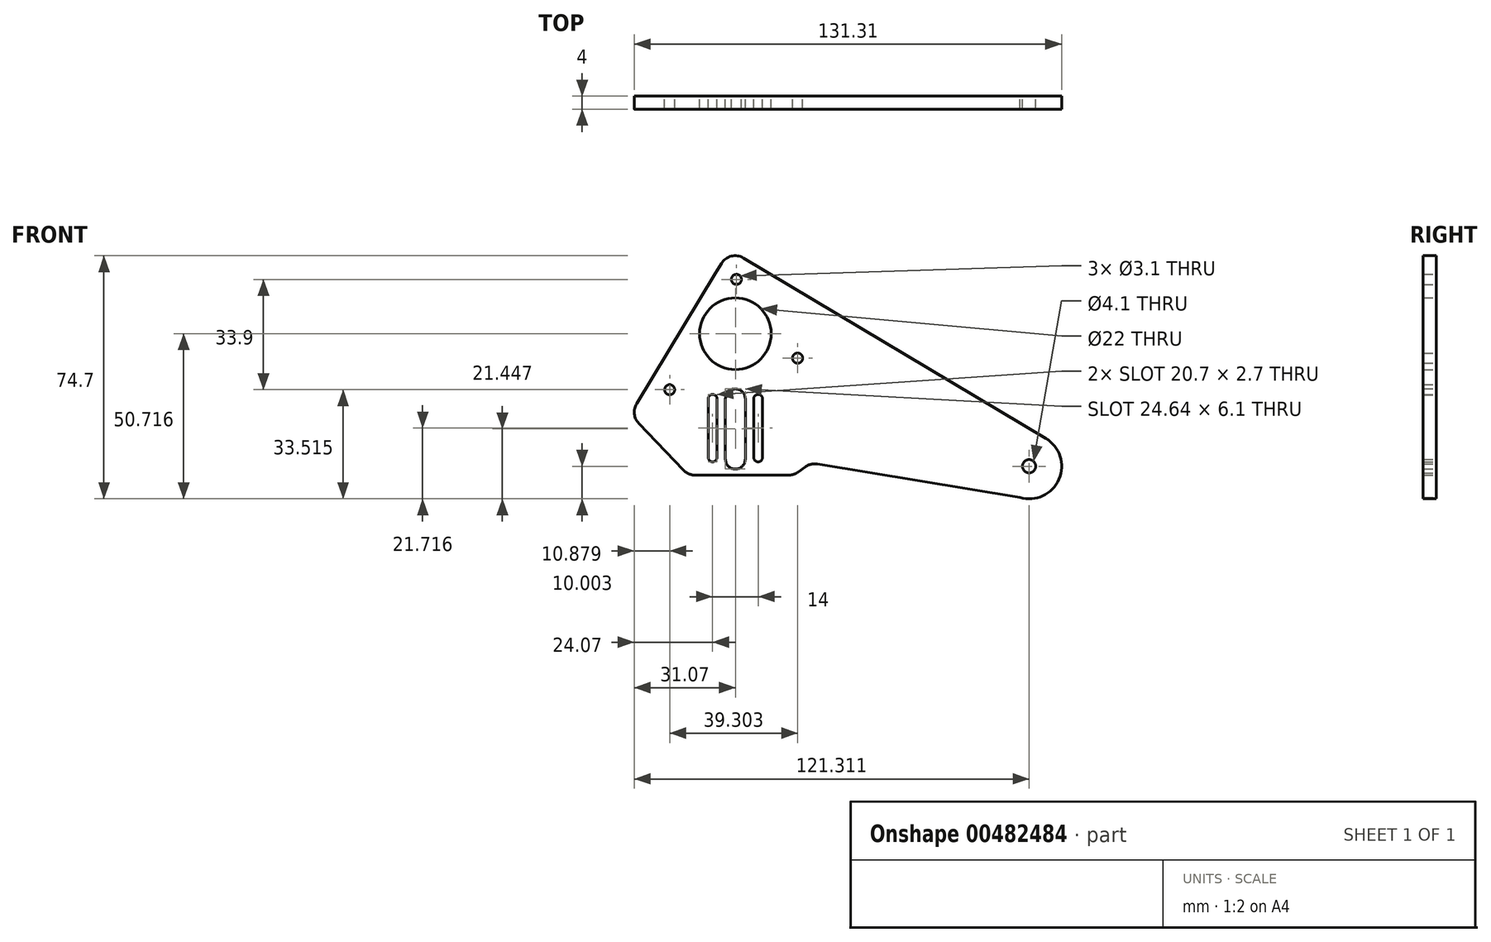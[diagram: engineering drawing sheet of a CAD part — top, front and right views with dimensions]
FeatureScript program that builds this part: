
annotation { "Feature Type Name" : "Feature", "Feature Type Description" : "" }
export const myFeature = defineFeature(function(context is Context, id is Id, definition is map)
    precondition{}
    {
        {
            var Q0;
            Q0=qCreatedBy(makeId("Front.planeOp"),FACE);
            var sketch = newSketch(context, id + "F0", { "sketchPlane" : qUnion([Q0])});
            skPoint(sketch, "E0", {"position": v(52.1, -15.47) * mm});
            skArc(sketch, "E1", {"start": v(49.27, -25.06) * mm, "mid": v(61.26, -19.47) * mm, "end": v(57.23, -6.88) * mm});
            skLineSegment(sketch, "E2", {"start": v(-12.58, 34.77) * mm, "end": v(57.23, -6.88) * mm});
            skPoint(sketch, "E3", {"position": v(-38.14, 25.25) * mm});
            skLineSegment(sketch, "E4", {"start": v(-68.49, 3.74) * mm, "end": v(-44.28, 43.8) * mm});
            skLineSegment(sketch, "E5", {"start": v(49.27, -25.06) * mm, "end": v(-12.93, -14.77) * mm});
            skLineSegment(sketch, "E6", {"start": v(-16.65, -15.64) * mm, "end": v(-18.93, -17.27) * mm});
            skLineSegment(sketch, "E7", {"start": v(-54.08, -16.66) * mm, "end": v(-67.82, -2.3) * mm});
            skLineSegment(sketch, "E8", {"start": v(-12.58, 34.77) * mm, "end": v(-35.62, 48.52) * mm});
            skLineSegment(sketch, "E9", {"start": v(-42.46, 46.82) * mm, "end": v(-44.28, 43.8) * mm});
            skPoint(sketch, "E10", {"position": v(-37.8, 41.95) * mm});
            skCircle(sketch, "E11", {"center": v(-38.14, 25.25) * mm, "radius": 11 * mm, "construction": true});
            skCircle(sketch, "E12", {"center": v(-37.8, 41.95) * mm, "radius": 4 * mm, "construction": true});
            skLineSegment(sketch, "E13", {"start": v(-50.47, -18.2) * mm, "end": v(-21.84, -18.2) * mm});
            skCircle(sketch, "E14", {"center": v(-19.03, 17.74) * mm, "radius": 4 * mm, "construction": true});
            skPoint(sketch, "E15", {"position": v(-58.03, 8.04) * mm});
            skCircle(sketch, "E16", {"center": v(-37.8, 41.95) * mm, "radius": 1.55 * mm});
            skCircle(sketch, "E17", {"center": v(-38.14, 25.25) * mm, "radius": 11 * mm});
            skCircle(sketch, "E18", {"center": v(-19.03, 17.74) * mm, "radius": 1.55 * mm});
            skCircle(sketch, "E19", {"center": v(52.1, -15.47) * mm, "radius": 2.05 * mm});
            skPoint(sketch, "E20.visualSharp", {"position": v(-70.47, 0.46) * mm});
            skArc(sketch, "E20.filletArc", {"start": v(-68.49, 3.74) * mm, "mid": v(-69.18, 0.6) * mm, "end": v(-67.82, -2.3) * mm});
            skPoint(sketch, "E21.visualSharp", {"position": v(-39.88, 51.06) * mm});
            skArc(sketch, "E21.filletArc", {"start": v(-35.62, 48.52) * mm, "mid": v(-39.39, 49.08) * mm, "end": v(-42.46, 46.82) * mm});
            skPoint(sketch, "E22.visualSharp", {"position": v(-52.6, -18.2) * mm});
            skArc(sketch, "E22.filletArc", {"start": v(-54.08, -16.66) * mm, "mid": v(-52.43, -17.8) * mm, "end": v(-50.47, -18.2) * mm});
            skPoint(sketch, "E23.visualSharp", {"position": v(-20.23, -18.2) * mm});
            skArc(sketch, "E23.filletArc", {"start": v(-21.84, -18.2) * mm, "mid": v(-20.3, -17.96) * mm, "end": v(-18.93, -17.27) * mm});
            skPoint(sketch, "E24.visualSharp", {"position": v(-14.97, -14.43) * mm});
            skArc(sketch, "E24.filletArc", {"start": v(-12.93, -14.77) * mm, "mid": v(-14.88, -14.83) * mm, "end": v(-16.65, -15.64) * mm});
            skPoint(sketch, "E25", {"position": v(-58.33, 8.04) * mm});
            skCircle(sketch, "E26", {"center": v(-58.33, 8.04) * mm, "radius": 1.55 * mm});
            skLineSegment(sketch, "E27", {"start": v(-38.14, 33.91) * mm, "end": v(-38.14, 14.25) * mm, "construction": true});
            skPoint(sketch, "E28", {"position": v(-38.14, 5.25) * mm});
            skLineSegment(sketch, "E29", {"start": v(-38.14, -12.75) * mm, "end": v(-38.14, -13.3) * mm});
            skLineSegment(sketch, "E30", {"start": v(-38.14, 5.25) * mm, "end": v(-45.14, 5.25) * mm});
            skLineSegment(sketch, "E31.trimOffspring", {"start": v(-38.14, -12.75) * mm, "end": v(-38.14, -13.3) * mm, "construction": true});
            skArc(sketch, "E32.0.startCap", {"start": v(-41.19, 5.25) * mm, "mid": v(-38.14, 8.3) * mm, "end": v(-35.09, 5.25) * mm});
            skArc(sketch, "E32.0.endCap", {"start": v(-35.09, -13.3) * mm, "mid": v(-38.14, -16.34) * mm, "end": v(-41.19, -13.3) * mm});
            skLineSegment(sketch, "E32.0.left", {"start": v(-35.09, 5.25) * mm, "end": v(-35.09, -13.3) * mm});
            skLineSegment(sketch, "E32.0.right", {"start": v(-41.19, 5.25) * mm, "end": v(-41.19, -13.3) * mm});
            skArc(sketch, "E33.0.startCap", {"start": v(-32.49, 5.25) * mm, "mid": v(-31.14, 6.6) * mm, "end": v(-29.79, 5.25) * mm});
            skArc(sketch, "E33.0.endCap", {"start": v(-29.79, -12.75) * mm, "mid": v(-31.14, -14.1) * mm, "end": v(-32.49, -12.75) * mm});
            skLineSegment(sketch, "E33.0.left", {"start": v(-29.79, 5.25) * mm, "end": v(-29.79, -12.75) * mm});
            skLineSegment(sketch, "E33.0.right", {"start": v(-32.49, 5.25) * mm, "end": v(-32.49, -12.75) * mm});
            skArc(sketch, "E34.0.startCap", {"start": v(-46.49, 5.25) * mm, "mid": v(-45.14, 6.6) * mm, "end": v(-43.79, 5.25) * mm});
            skArc(sketch, "E34.0.endCap", {"start": v(-43.79, -12.75) * mm, "mid": v(-45.14, -14.1) * mm, "end": v(-46.49, -12.75) * mm});
            skLineSegment(sketch, "E34.0.left", {"start": v(-43.79, 5.25) * mm, "end": v(-43.79, -12.75) * mm});
            skLineSegment(sketch, "E34.0.right", {"start": v(-46.49, 5.25) * mm, "end": v(-46.49, -12.75) * mm});
            skLineSegment(sketch, "E35", {"start": v(-38.14, 5.25) * mm, "end": v(-38.14, -12.75) * mm, "construction": true});
            skPoint(sketch, "E36", {"position": v(-38.14, -3.75) * mm});
            skSolve(sketch);
        }
        {
            var Q0;
            Q0 = qSketchRegion(id + "F0", true);
            extrude(context, id + "F1", {"entities" : qUnion([Q0]), "depth" : 4 * mm, "offsetDistance" : 25 * mm});
        }
    });
